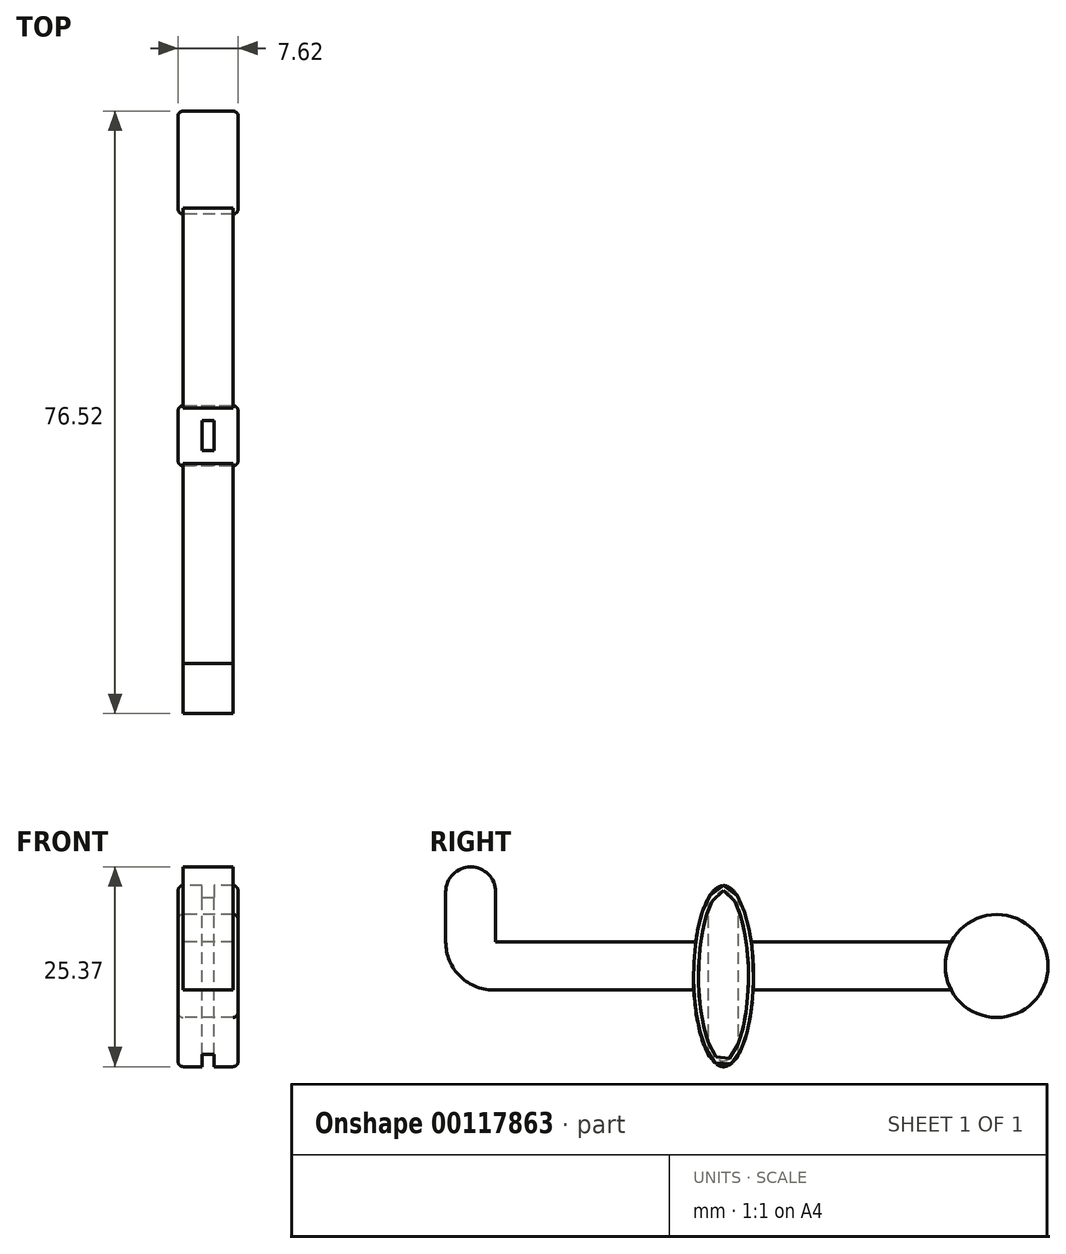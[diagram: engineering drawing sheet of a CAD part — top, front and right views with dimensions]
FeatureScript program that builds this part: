
annotation { "Feature Type Name" : "Feature", "Feature Type Description" : "" }
export const myFeature = defineFeature(function(context is Context, id is Id, definition is map)
    precondition{}
    {
        {
            var Q0;
            Q0=qCreatedBy(makeId("Right.planeOp"),FACE);
            var sketch = newSketch(context, id + "F0", { "sketchPlane" : qUnion([Q0])});
            skEllipse(sketch, "E0", {"center": v(0, -1.29) * mm, "majorRadius": 11.5 * mm, "minorRadius": 3.81 * mm, "majorAxis": v(0, 1)});
            skLineSegment(sketch, "E1.top", {"start": v(-28.93, 3.05) * mm, "end": v(-3.53, 3.05) * mm});
            skLineSegment(sketch, "E1.left", {"start": v(-28.93, 0) * mm, "end": v(-28.93, 3.05) * mm});
            skLineSegment(sketch, "E2.MirrorCS", {"start": v(-28.93, -3.05) * mm, "end": v(-3.53, -3.05) * mm});
            skLineSegment(sketch, "E3.MirrorCS", {"start": v(-28.93, -0.24) * mm, "end": v(-28.93, -3.3) * mm});
            skLineSegment(sketch, "E4.MirrorCS", {"start": v(28.93, -3.05) * mm, "end": v(3.53, -3.05) * mm});
            skLineSegment(sketch, "E5.MirrorCS", {"start": v(28.93, 3.05) * mm, "end": v(3.53, 3.05) * mm});
            skLineSegment(sketch, "E6", {"start": v(-28.93, 3.05) * mm, "end": v(-28.93, -3.05) * mm});
            skLineSegment(sketch, "E7", {"start": v(-28.93, 3.05) * mm, "end": v(-35.28, 3.05) * mm});
            skLineSegment(sketch, "E8", {"start": v(-35.28, 3.05) * mm, "end": v(-35.28, 9.4) * mm});
            skArc(sketch, "E9", {"start": v(-35.28, 3.05) * mm, "mid": v(-33.4, -1.35) * mm, "end": v(-28.93, -3.05) * mm});
            skLineSegment(sketch, "E10", {"start": v(-28.93, 3.05) * mm, "end": v(-28.93, 9.4) * mm});
            skArc(sketch, "E11", {"start": v(-28.93, 9.4) * mm, "mid": v(-32.1, 12.58) * mm, "end": v(-35.28, 9.4) * mm});
            skCircle(sketch, "E12", {"center": v(34.7, 0) * mm, "radius": 6.54 * mm});
            skLineSegment(sketch, "E13", {"start": v(0, 10.21) * mm, "end": v(0, -12.79) * mm});
            skSolve(sketch);
        }
        {
            var Q0;
            {var subQ1=sQuery(id+"F0.wireOp",EDGE,"E1.top");Q0=makeQuery(id+"F0.imprint","IMPRINT",FACE,{"disambiguationData":[TD([[makeQuery(id+"F0.imprint","IMPRINT",EDGE,{"derivedFrom":subQ1}),-1.0]])]});}
            var Q1;
            {var subQ0=sQuery(id+"F0.wireOp",EDGE,"E5.MirrorCS");Q1=makeQuery(id+"F0.imprint","IMPRINT",FACE,{"disambiguationData":[TD([[makeQuery(id+"F0.imprint","IMPRINT",EDGE,{"derivedFrom":subQ0}),1.0]])]});}
            var Q2;
            {var subQ0=sQuery(id+"F0.wireOp",EDGE,"E7");Q2=makeQuery(id+"F0.imprint","IMPRINT",FACE,{"disambiguationData":[TD([[makeQuery(id+"F0.imprint","IMPRINT",EDGE,{"derivedFrom":subQ0}),1.0]])]});}
            var Q3;
            Q3=makeQuery(id+"F0.imprint","IMPRINT",FACE,{"disambiguationData":[TD([[makeQuery(id+"F0.imprint","IMPRINT",EDGE,{"derivedFrom":sQuery(id+"F0.wireOp",EDGE,"E7")}),-1.0]])]});
            extrude(context, id + "F1", {"entities" : qUnion([Q0, Q1, Q2, Q3]), "endBound" : BoundingType.SYMMETRIC, "depth" : 6.35 * mm});
        }
        {
            var Q0;
            {var subQ0=sQuery(id+"F0.wireOp",EDGE,"E13");Q0=makeQuery(id+"F0.imprint","IMPRINT",FACE,{"disambiguationData":[TD([[makeQuery(id+"F0.imprint","IMPRINT",EDGE,{"derivedFrom":subQ0}),1.0]])]});}
            var Q1;
            {var subQ2=sQuery(id+"F0.wireOp",EDGE,"E13");Q1=makeQuery(id+"F0.imprint","IMPRINT",FACE,{"disambiguationData":[TD([[makeQuery(id+"F0.imprint","IMPRINT",EDGE,{"derivedFrom":subQ2}),-1.0]])]});}
            var Q2;
            {var subQ0=sQuery(id+"F0.wireOp",EDGE,"E12");var subQ1=makeQuery(id+"F0.imprint","INTERSECT",VERTEX,{"derivedFrom":[sQuery(id+"F0.wireOp",EDGE,"E4.MirrorCS"),subQ0]});Q2=makeQuery(id+"F0.imprint","IMPRINT",FACE,{"disambiguationData":[TD([[makeQuery(id+"F0.imprint","IMPRINT",EDGE,{"disambiguationData":[TD([[subQ1,1.0]])],"derivedFrom":subQ0}),1.0]])]});}
            extrude(context, id + "F2", {"entities" : qUnion([Q0, Q1, Q2]), "endBound" : BoundingType.SYMMETRIC, "depth" : 7.62 * mm});
        }
        {
            var Q0;
            Q0=makeQuery(id+"F2.opExtrude","CAP_FACE",FACE,{"disambiguationData":[OSD([sQuery(id+"F0.wireOp",EDGE,"E0")])],"isStart":false});
            var Q1;
            Q1=makeQuery(id+"F2.opExtrude","CAP_EDGE",EDGE,{"disambiguationData":[OSD([sQuery(id+"F0.wireOp",EDGE,"E12")])],"isStart":false});
            var Q2;
            Q2=makeQuery(id+"F2.opExtrude","CAP_EDGE",EDGE,{"disambiguationData":[OSD([sQuery(id+"F0.wireOp",EDGE,"E12")])],"isStart":true});
            var Q3;
            Q3=makeQuery(id+"F2.opExtrude","CAP_EDGE",EDGE,{"disambiguationData":[OSD([sQuery(id+"F0.wireOp",EDGE,"E0")])],"isStart":true});
            fillet(context, id + "F3", {"entities" : qUnion([Q0, Q1, Q2, Q3]), "radius" : 0.64 * mm, "tangentPropagation" : true, "allowEdgeOverflow" : false});
        }
        {
            var Q0;
            Q0=qCreatedBy(makeId("Top.planeOp"),FACE);
            var sketch = newSketch(context, id + "F4", { "sketchPlane" : qUnion([Q0])});
            skLineSegment(sketch, "E14", {"start": v(-0.76, 1.9) * mm, "end": v(-0.76, -1.9) * mm});
            skLineSegment(sketch, "E15", {"start": v(0.76, 1.9) * mm, "end": v(0.76, -1.9) * mm});
            skLineSegment(sketch, "E16", {"start": v(-0.76, 1.9) * mm, "end": v(0.76, 1.9) * mm});
            skLineSegment(sketch, "E17", {"start": v(-0.76, -1.9) * mm, "end": v(0.76, -1.9) * mm});
            skSolve(sketch);
        }
        {
            var Q0;
            Q0 = qSketchRegion(id + "F4", true);
            extrude(context, id + "F5", {"entities" : qUnion([Q0]), "operationType" : NewBodyOperationType.REMOVE, "endBound" : BoundingType.SYMMETRIC, "oppositeDirection" : true, "depth" : 79.78 * mm});
        }
    });
